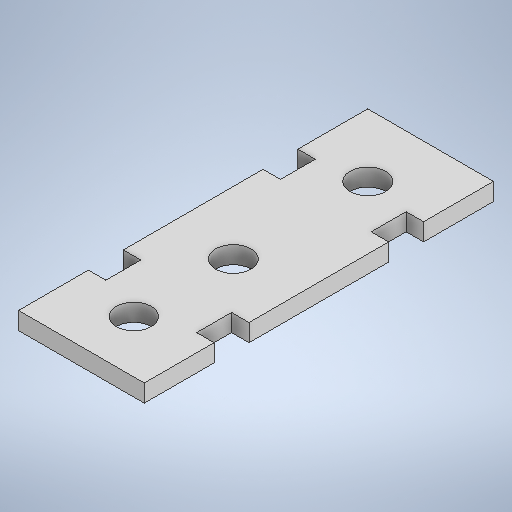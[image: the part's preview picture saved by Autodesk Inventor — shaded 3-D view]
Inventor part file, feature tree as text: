
AUTODESK INVENTOR PART (.ipt)
format: ipt  version: 2025.2 (Build 292293000, 293)  size: 256,000 bytes
history: native  units: mm
features: extrude x1, sketch x1
ambient origin geometry x8: Origin, YZ Plane, XZ Plane, XY Plane, X Axis, Y Axis, Z Axis, Center Point
bodies: Solid1 (feature_tree)
feature tree (2):
  extrude  "Extrusion1"  Depth=100.0mm
  sketch  "Sketch2"  dims[d0=36.0mm d1=100.0mm d2=20.0mm d3=20.0mm d4=10.0mm d5=5.0mm d6=10.0mm d7=5.0mm d8=5.0mm d9=15.0mm d11=28.5mm d12=10.1mm d13=38.5mm d14=10.1mm d15=5.0mm d16=0.0mm]
